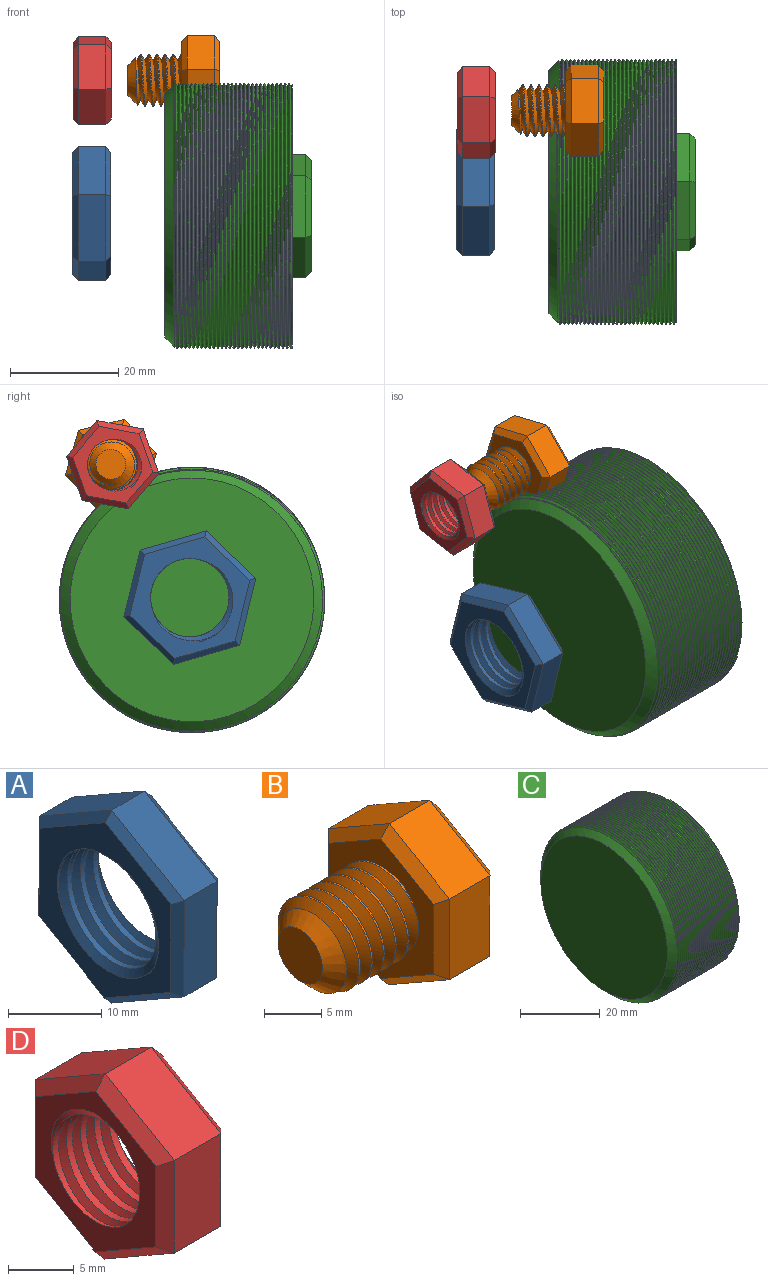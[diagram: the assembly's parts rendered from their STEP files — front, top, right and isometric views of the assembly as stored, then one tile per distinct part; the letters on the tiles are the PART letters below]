
ASSEMBLY  parts=4 mates=2
PART A: 23 faces, bbox 9.3x22.7x26 mm
  f0: cylinder r=7.24mm len=14.48mm, axis (1,0,0), area 111.6mm2, adj f7,f8,f21,f22
  f1: plane 10.98x6.38mm, normal (0,-0.5,0.86), area 63.5mm2, adj f2,f6,f14,f18
  f2: plane 12.7x5mm, normal (0,-1,0), area 63.5mm2, adj f1,f3,f12,f16
  f3: plane 11.02x6.32mm, normal (0,-0.5,-0.87), area 63.5mm2, adj f2,f4,f10,f15
  f4: plane 10.98x6.38mm, normal (0,0.5,-0.86), area 63.5mm2, adj f3,f5,f9,f17
  f5: plane 12.7x5mm, normal (0,1,0), area 63.5mm2, adj f4,f6,f11,f19
  f6: plane 11.02x6.32mm, normal (0,0.5,0.87), area 63.5mm2, adj f1,f5,f13,f20
  f7: plane 23.73x20.67mm, normal (-1,0,0), area 164.4mm2, adj f0,f9,f10,f11,f12,f13,f14,f21
  f8: plane 23.73x20.67mm, normal (1,0,0), area 164.4mm2, adj f0,f15,f16,f17,f18,f19,f20,f21
  f9: plane 10.99x6.96mm, normal (-0.71,0.36,-0.61), area 17.1mm2, adj f4,f7,f10,f11
  f10: plane 11.02x6.9mm, normal (-0.71,-0.35,-0.61), area 17.1mm2, adj f3,f7,f9,f12
  f11: plane 12.7x1.03mm, normal (-0.71,0.71,0), area 17.1mm2, adj f5,f7,f9,f13
  f12: plane 12.7x1.03mm, normal (-0.71,-0.71,0), area 17.1mm2, adj f2,f7,f10,f14
  f13: plane 11.02x6.9mm, normal (-0.71,0.35,0.61), area 17.1mm2, adj f6,f7,f11,f14
  f14: plane 10.99x6.96mm, normal (-0.71,-0.36,0.61), area 17.1mm2, adj f1,f7,f12,f13
  f15: plane 11.02x6.9mm, normal (0.71,-0.35,-0.61), area 17.1mm2, adj f3,f8,f16,f17
  f16: plane 12.7x1.03mm, normal (0.71,-0.71,0), area 17.1mm2, adj f2,f8,f15,f18
  f17: plane 10.99x6.96mm, normal (0.71,0.36,-0.61), area 17.1mm2, adj f4,f8,f15,f19
  f18: plane 10.99x6.96mm, normal (0.71,-0.36,0.61), area 17.1mm2, adj f1,f8,f16,f20
  f19: plane 12.7x1.03mm, normal (0.71,0.71,0), area 17.1mm2, adj f5,f8,f17,f20
  f20: plane 11.02x6.9mm, normal (0.71,0.35,0.61), area 17.1mm2, adj f6,f8,f18,f19
  f21: bspline ~19.31x16.73mm, area 223mm2, adj f0,f7,f8,f22
  f22: bspline ~19.31x16.73mm, area 223mm2, adj f0,f7,f8,f21
PART B: 25 faces, bbox 17.8x15.9x18.1 mm
  f0: cylinder r=4.75mm len=9.5mm, axis (1,0,0), area 28.1mm2, adj f1,f2,f4,f12
  f1: bspline ~10.97x9.91mm, area 196.7mm2, adj f0,f2,f4,f12
  f2: bspline ~10.97x10.66mm, area 196.6mm2, adj f0,f1,f4,f12
  f3: plane 5.5x5.5mm, normal (-1,0,0), area 23.8mm2, adj f4
  f4: cone r=4.75mm half-angle=45deg, axis (1,0,0), area 47.4mm2, adj f0,f1,f2,f3
  f5: plane 7.48x5mm, normal (0,-0.5,0.86), area 43.3mm2, adj f6,f10,f18,f22
  f6: plane 8.66x5mm, normal (0,-1,0), area 43.3mm2, adj f5,f7,f16,f20
  f7: plane 7.52x5mm, normal (0,-0.5,-0.87), area 43.3mm2, adj f6,f8,f14,f19
  f8: plane 7.48x5mm, normal (0,0.5,-0.86), area 43.3mm2, adj f7,f9,f13,f21
  f9: plane 8.66x5mm, normal (0,1,0), area 43.3mm2, adj f8,f10,f15,f23
  f10: plane 7.52x5mm, normal (0,0.5,0.87), area 43.3mm2, adj f5,f9,f17,f24
  f11: plane 15.01x13.03mm, normal (1,0,0), area 146.4mm2, adj f13,f14,f15,f16,f17,f18
  f12: plane 15.83x13.85mm, normal (-1,0,0), area 89.2mm2, adj f0,f1,f2,f19,f20,f21,f22,f23
  f13: plane 7.49x4.93mm, normal (0.71,0.36,-0.61), area 11.4mm2, adj f8,f11,f14,f15
  f14: plane 7.52x4.88mm, normal (0.71,-0.35,-0.61), area 11.4mm2, adj f7,f11,f13,f16
  f15: plane 8.66x1.03mm, normal (0.71,0.71,0), area 11.4mm2, adj f9,f11,f13,f17
  f16: plane 8.66x1.03mm, normal (0.71,-0.71,0), area 11.4mm2, adj f6,f11,f14,f18
  f17: plane 7.52x4.88mm, normal (0.71,0.35,0.61), area 11.4mm2, adj f10,f11,f15,f18
  f18: plane 7.49x4.93mm, normal (0.71,-0.36,0.61), area 11.4mm2, adj f5,f11,f16,f17
  f19: plane 7.52x4.88mm, normal (-0.71,-0.35,-0.61), area 11.4mm2, adj f7,f12,f20,f21
  f20: plane 8.66x1.03mm, normal (-0.71,-0.71,0), area 11.4mm2, adj f6,f12,f19,f22
  f21: plane 7.49x4.93mm, normal (-0.71,0.36,-0.61), area 11.4mm2, adj f8,f12,f19,f23
  f22: plane 7.49x4.93mm, normal (-0.71,-0.36,0.61), area 11.4mm2, adj f5,f12,f20,f24
  f23: plane 8.66x1.03mm, normal (-0.71,0.71,0), area 11.4mm2, adj f9,f12,f21,f24
  f24: plane 7.52x4.88mm, normal (-0.71,0.35,0.61), area 11.4mm2, adj f10,f12,f22,f23
PART C: 20 faces, bbox 27.7x57.3x49.7 mm
  f0: cylinder r=24.5mm len=49mm, axis (1,0,0), area 772.9mm2, adj f2,f3,f4,f5,f6
  f1: plane 45x45mm, normal (-1,0,0), area 1590.4mm2, adj f3
  f2: plane 49.68x49.44mm, normal (1,0,0), area 1520.3mm2, adj f0,f4,f5,f7,f8,f9,f10,f11
  f3: cone r=24.5mm half-angle=45deg, axis (1,0,0), area 364mm2, adj f0,f1,f5,f6
  f4: plane 0.57x0.33mm, normal (0,1,0), area 0.1mm2, adj f0,f2,f6
  f5: bspline ~56.58x49mm, area 2904.1mm2, adj f0,f2,f3,f6
  f6: bspline ~56.58x49mm, area 2870.6mm2, adj f0,f3,f4,f5
  f7: plane 9.98x5.81mm, normal (0,-0.5,0.86), area 28.9mm2, adj f2,f8,f12,f19
  f8: plane 11.55x2.5mm, normal (0,-1,0), area 28.9mm2, adj f2,f7,f9,f17
  f9: plane 10.02x5.74mm, normal (0,-0.5,-0.87), area 28.9mm2, adj f2,f8,f10,f15
  f10: plane 9.98x5.81mm, normal (0,0.5,-0.86), area 28.9mm2, adj f2,f9,f11,f14
  f11: plane 11.55x2.5mm, normal (0,1,0), area 28.9mm2, adj f2,f10,f12,f16
  f12: plane 10.02x5.74mm, normal (0,0.5,0.87), area 28.9mm2, adj f2,f7,f11,f18
  f13: plane 20.78x18.04mm, normal (1,0,0), area 280.6mm2, adj f14,f15,f16,f17,f18,f19
  f14: plane 9.98x6.38mm, normal (0.71,0.36,-0.61), area 15.5mm2, adj f10,f13,f15,f16
  f15: plane 10.02x6.32mm, normal (0.71,-0.35,-0.61), area 15.5mm2, adj f9,f13,f14,f17
  f16: plane 11.55x1.04mm, normal (0.71,0.71,0), area 15.5mm2, adj f11,f13,f14,f18
  f17: plane 11.55x1.04mm, normal (0.71,-0.71,0), area 15.5mm2, adj f8,f13,f15,f19
  f18: plane 10.02x6.32mm, normal (0.71,0.35,0.61), area 15.5mm2, adj f12,f13,f16,f19
  f19: plane 9.98x6.38mm, normal (0.71,-0.36,0.61), area 15.5mm2, adj f7,f13,f17,f18
PART D: 23 faces, bbox 9.1x15.4x17.7 mm
  f0: plane 7.49x5mm, normal (0,-0.5,0.86), area 43.3mm2, adj f1,f5,f13,f17
  f1: plane 8.66x5mm, normal (0,-1,0), area 43.3mm2, adj f0,f2,f11,f15
  f2: plane 7.51x5mm, normal (0,-0.5,-0.87), area 43.3mm2, adj f1,f3,f9,f14
  f3: plane 7.49x5mm, normal (0,0.5,-0.86), area 43.3mm2, adj f2,f4,f8,f16
  f4: plane 8.66x5mm, normal (0,1,0), area 43.3mm2, adj f3,f5,f10,f18
  f5: plane 7.51x5mm, normal (0,0.5,0.87), area 43.3mm2, adj f0,f4,f12,f19
  f6: plane 15.37x13.38mm, normal (-1,0,0), area 71.4mm2, adj f8,f9,f10,f11,f12,f13,f20,f21
  f7: plane 15.37x13.38mm, normal (1,0,0), area 71.4mm2, adj f14,f15,f16,f17,f18,f19,f20,f21
  f8: plane 7.49x4.93mm, normal (-0.71,0.36,-0.61), area 11.4mm2, adj f3,f6,f9,f10
  f9: plane 7.51x4.89mm, normal (-0.71,-0.35,-0.61), area 11.4mm2, adj f2,f6,f8,f11
  f10: plane 8.66x1.02mm, normal (-0.71,0.71,0), area 11.4mm2, adj f4,f6,f8,f12
  f11: plane 8.66x1.02mm, normal (-0.71,-0.71,0), area 11.4mm2, adj f1,f6,f9,f13
  f12: plane 7.51x4.89mm, normal (-0.71,0.35,0.61), area 11.4mm2, adj f5,f6,f10,f13
  f13: plane 7.49x4.93mm, normal (-0.71,-0.36,0.61), area 11.4mm2, adj f0,f6,f11,f12
  f14: plane 7.51x4.89mm, normal (0.71,-0.35,-0.61), area 11.4mm2, adj f2,f7,f15,f16
  f15: plane 8.66x1.02mm, normal (0.71,-0.71,0), area 11.4mm2, adj f1,f7,f14,f17
  f16: plane 7.49x4.93mm, normal (0.71,0.36,-0.61), area 11.4mm2, adj f3,f7,f14,f18
  f17: plane 7.49x4.93mm, normal (0.71,-0.36,0.61), area 11.4mm2, adj f0,f7,f15,f19
  f18: plane 8.66x1.02mm, normal (0.71,0.71,0), area 11.4mm2, adj f4,f7,f16,f19
  f19: plane 7.51x4.89mm, normal (0.71,0.35,0.61), area 11.4mm2, adj f5,f7,f17,f18
  f20: cylinder r=4.66mm len=9.32mm, axis (1,0,0), area 85.4mm2, adj f6,f7,f21,f22
  f21: bspline ~12.5x10.82mm, area 128.4mm2, adj f6,f7,f20,f22
  f22: bspline ~12.5x10.82mm, area 128.5mm2, adj f6,f7,f20,f21
PLACE A rot(axis=(0,0.6,-0.8),180deg) t=(-55.27,-6.86,23.48)mm fixed
PLACE B rot(axis=(-1,0,0),43.8deg) t=(-31.66,7.73,48.08)mm
PLACE C rot(axis=(1,0,0),109.9deg) t=(-14.77,-7.25,23.06)mm
PLACE D rot(axis=(1,0,0),100.2deg) t=(-48.16,7.38,48.02)mm fixed
MATE cylindrical C.f0 <-> A.f7  axis (-1,0,0) through (-38.27,-7.25,23.06)mm
MATE cylindrical B.f0 <-> D.f6  axis (-1,0,0) through (-45.16,7.73,48.08)mm
